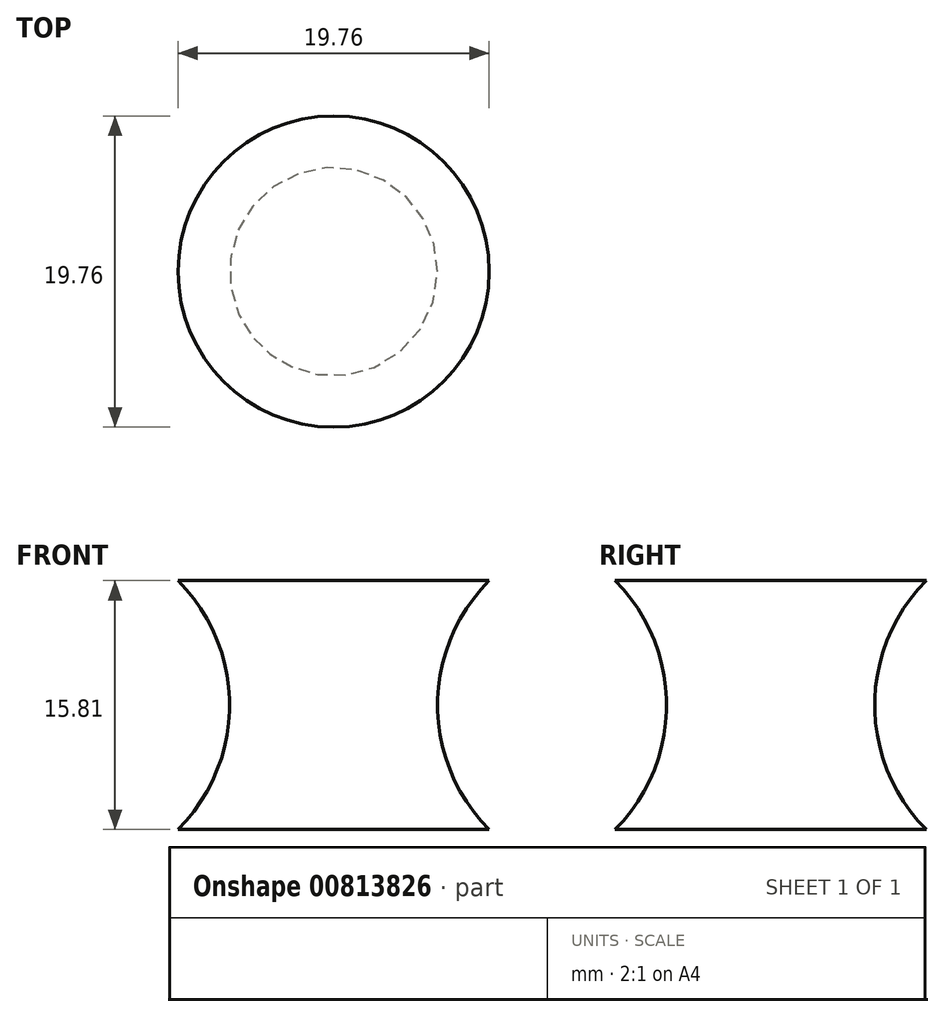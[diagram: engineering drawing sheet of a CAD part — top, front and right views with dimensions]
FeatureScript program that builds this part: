
annotation { "Feature Type Name" : "Feature", "Feature Type Description" : "" }
export const myFeature = defineFeature(function(context is Context, id is Id, definition is map)
    precondition{}
    {
        {
            var Q0;
            Q0=qCreatedBy(makeId("Front.planeOp"),FACE);
            var sketch = newSketch(context, id + "F0", { "sketchPlane" : qUnion([Q0])});
            skLineSegment(sketch, "E0", {"start": v(-27.57, 20.95) * mm, "end": v(-27.57, 5.14) * mm});
            skLineSegment(sketch, "E1", {"start": v(-27.57, 20.95) * mm, "end": v(-17.69, 20.95) * mm});
            skLineSegment(sketch, "E2", {"start": v(-27.57, 5.14) * mm, "end": v(-17.69, 5.14) * mm});
            skArc(sketch, "E3", {"start": v(-17.69, 20.95) * mm, "mid": v(-20.96, 13.04) * mm, "end": v(-17.69, 5.14) * mm});
            skSolve(sketch);
        }
        {
            var Q0;
            Q0=makeQuery(id+"F0.imprint","IMPRINT",FACE,{"disambiguationData":[TD([[makeQuery(id+"F0.imprint","IMPRINT",EDGE,{"derivedFrom":sQuery(id+"F0.wireOp",EDGE,"E0")}),1.0]])]});
            var Q1;
            Q1=sQuery(id+"F0.wireOp",EDGE,"E0");
            revolve(context, id + "F1", {"surfaceOperationType" : NewSurfaceOperationType.NEW, "entities" : qUnion([Q0]), "axis" : qUnion([Q1]), "revolveType" : RevolveType.FULL});
        }
    });
